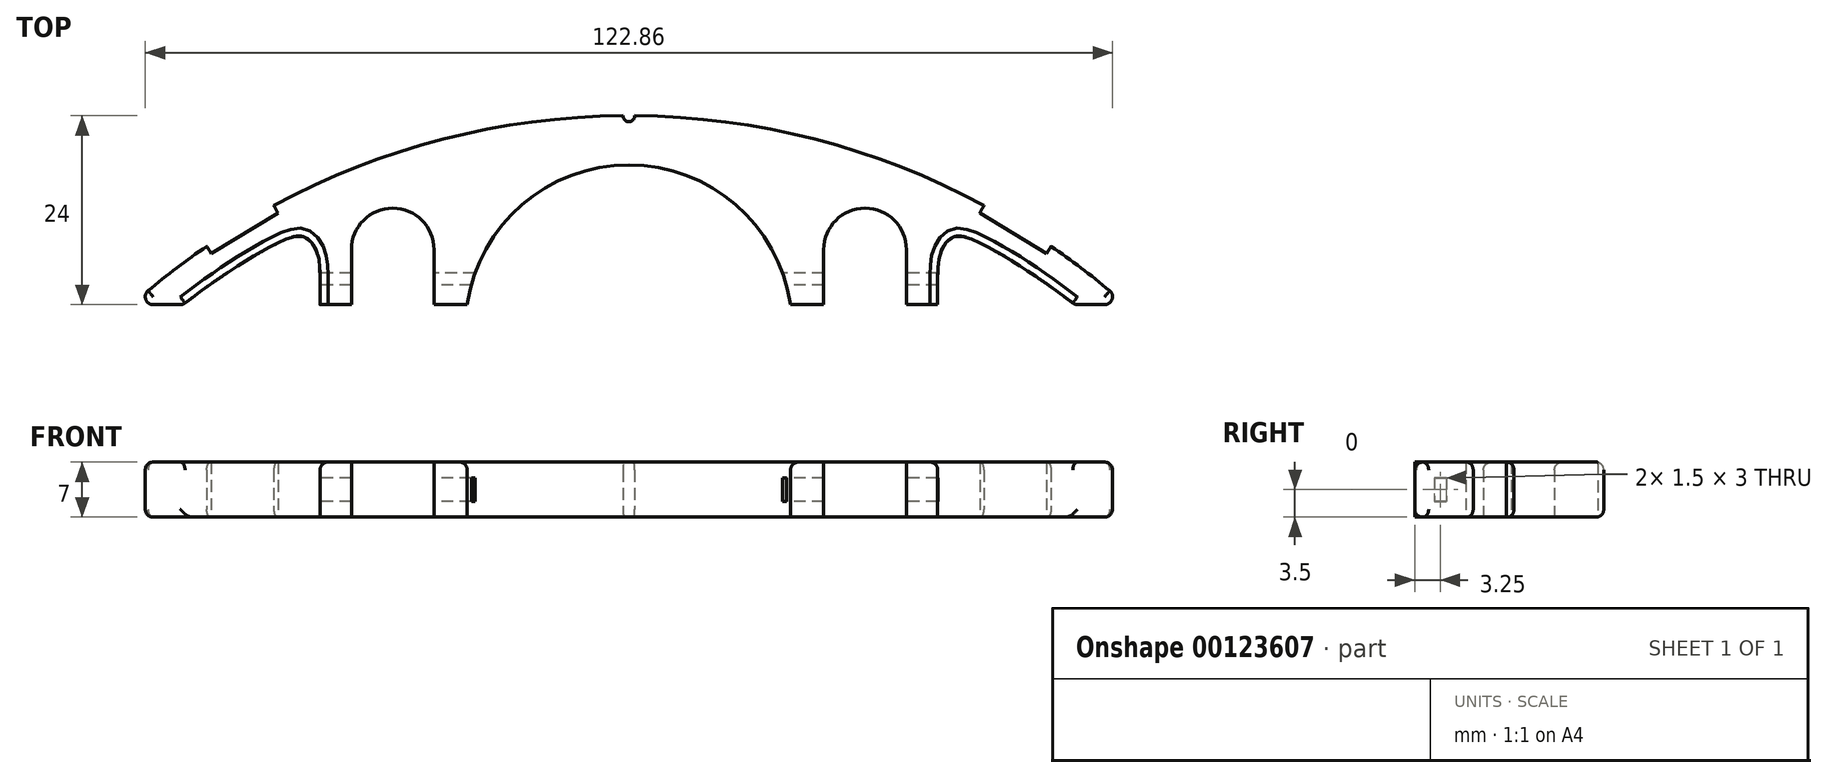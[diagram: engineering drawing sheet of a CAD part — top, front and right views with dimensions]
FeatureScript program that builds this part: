
annotation { "Feature Type Name" : "Feature", "Feature Type Description" : "" }
export const myFeature = defineFeature(function(context is Context, id is Id, definition is map)
    precondition{}
    {
        {
            var Q0;
            Q0=qCreatedBy(makeId("Top.planeOp"),FACE);
            var sketch = newSketch(context, id + "F0", { "sketchPlane" : qUnion([Q0])});
            skCircle(sketch, "E0", {"center": v(0, -78) * mm, "radius": 95 * mm});
            skSolve(sketch);
        }
        {
            var Q0;
            Q0=qCreatedBy(makeId("Top.planeOp"),FACE);
            var sketch = newSketch(context, id + "F1", { "sketchPlane" : qUnion([Q0])});
            skCircle(sketch, "E1", {"center": v(-30, 0) * mm, "radius": 5.25 * mm});
            skSolve(sketch);
        }
        {
            var Q0;
            Q0=qCreatedBy(makeId("Top.planeOp"),FACE);
            var sketch = newSketch(context, id + "F2", { "sketchPlane" : qUnion([Q0])});
            skCircle(sketch, "E2", {"center": v(30, 0) * mm, "radius": 5.25 * mm});
            skSolve(sketch);
        }
        {
            var Q0;
            Q0=qCreatedBy(makeId("Top.planeOp"),FACE);
            var sketch = newSketch(context, id + "F3", { "sketchPlane" : qUnion([Q0])});
            skCircle(sketch, "E3", {"center": v(0, -10) * mm, "radius": 20.75 * mm});
            skSolve(sketch);
        }
        {
            var Q0;
            Q0=qCreatedBy(makeId("Top.planeOp"),FACE);
            var sketch = newSketch(context, id + "F4", { "sketchPlane" : qUnion([Q0])});
            skLineSegment(sketch, "E4.bottom", {"start": v(-90, -20) * mm, "end": v(90, -20) * mm});
            skLineSegment(sketch, "E4.top", {"start": v(-90, -160) * mm, "end": v(90, -160) * mm});
            skLineSegment(sketch, "E4.left", {"start": v(-90, -20) * mm, "end": v(-90, -160) * mm});
            skLineSegment(sketch, "E4.right", {"start": v(90, -20) * mm, "end": v(90, -160) * mm});
            skSolve(sketch);
        }
        {
            var Q0;
            Q0=qCreatedBy(makeId("Top.planeOp"),FACE);
            var sketch = newSketch(context, id + "F5", { "sketchPlane" : qUnion([Q0])});
            skLineSegment(sketch, "E5.bottom", {"start": v(-20.75, -10) * mm, "end": v(20.75, -10) * mm});
            skLineSegment(sketch, "E5.top", {"start": v(-20.75, -51.5) * mm, "end": v(20.75, -51.5) * mm});
            skLineSegment(sketch, "E5.left", {"start": v(-20.75, -10) * mm, "end": v(-20.75, -51.5) * mm});
            skLineSegment(sketch, "E5.right", {"start": v(20.75, -10) * mm, "end": v(20.75, -51.5) * mm});
            skSolve(sketch);
        }
        {
            var Q0;
            Q0=qCreatedBy(makeId("Top.planeOp"),FACE);
            var sketch = newSketch(context, id + "F6", { "sketchPlane" : qUnion([Q0])});
            skLineSegment(sketch, "E6.bottom", {"start": v(-35.25, 0) * mm, "end": v(-24.75, 0) * mm});
            skLineSegment(sketch, "E6.top", {"start": v(-35.25, -25) * mm, "end": v(-24.75, -25) * mm});
            skLineSegment(sketch, "E6.left", {"start": v(-35.25, 0) * mm, "end": v(-35.25, -25) * mm});
            skLineSegment(sketch, "E6.right", {"start": v(-24.75, 0) * mm, "end": v(-24.75, -25) * mm});
            skSolve(sketch);
        }
        {
            var Q0;
            Q0=qCreatedBy(makeId("Top.planeOp"),FACE);
            var sketch = newSketch(context, id + "F7", { "sketchPlane" : qUnion([Q0])});
            skLineSegment(sketch, "E7.bottom", {"start": v(24.75, 0) * mm, "end": v(35.25, 0) * mm});
            skLineSegment(sketch, "E7.top", {"start": v(24.75, -25) * mm, "end": v(35.25, -25) * mm});
            skLineSegment(sketch, "E7.left", {"start": v(24.75, 0) * mm, "end": v(24.75, -25) * mm});
            skLineSegment(sketch, "E7.right", {"start": v(35.25, 0) * mm, "end": v(35.25, -25) * mm});
            skSolve(sketch);
        }
        {
            var Q0;
            Q0=qCreatedBy(makeId("Top.planeOp"),FACE);
            var sketch = newSketch(context, id + "F8", { "sketchPlane" : qUnion([Q0])});
            skCircle(sketch, "E8", {"center": v(0, -155) * mm, "radius": 153 * mm});
            skSolve(sketch);
        }
        {
            var Q0;
            Q0 = qSketchRegion(id + "F0", true);
            extrude(context, id + "F9", {"entities" : qUnion([Q0]), "depth" : 7 * mm});
        }
        {
            var Q0;
            Q0 = qSketchRegion(id + "F1", true);
            var Q1;
            Q1 = qSketchRegion(id + "F2", true);
            var Q2;
            Q2 = qSketchRegion(id + "F3", true);
            var Q3;
            Q3 = qSketchRegion(id + "F4", true);
            var Q4;
            Q4 = qSketchRegion(id + "F6", true);
            var Q5;
            Q5 = qSketchRegion(id + "F7", true);
            var Q6;
            Q6 = qSketchRegion(id + "F5", true);
            extrude(context, id + "F10", {"entities" : qUnion([Q0, Q1, Q2, Q3, Q4, Q5, Q6]), "depth" : 25 * mm});
        }
        {
            var Q0;
            Q0=makeQuery(id+"F10.opExtrude","SWEPT_BODY",BODY,{"disambiguationData":[OSD([sQuery(id+"F1.wireOp",EDGE,"E1")])]});
            var Q1;
            Q1=makeQuery(id+"F10.opExtrude","SWEPT_BODY",BODY,{"disambiguationData":[OSD([sQuery(id+"F2.wireOp",EDGE,"E2")])]});
            var Q2;
            Q2=makeQuery(id+"F10.opExtrude","SWEPT_BODY",BODY,{"disambiguationData":[OSD([sQuery(id+"F3.wireOp",EDGE,"E3")])]});
            var Q3;
            Q3=makeQuery(id+"F10.opExtrude","SWEPT_BODY",BODY,{"disambiguationData":[OSD([sQuery(id+"F4.wireOp",EDGE,"E4.bottom"),sQuery(id+"F4.wireOp",EDGE,"E4.top"),sQuery(id+"F4.wireOp",EDGE,"E4.left"),sQuery(id+"F4.wireOp",EDGE,"E4.right")])]});
            var Q4;
            Q4=makeQuery(id+"F10.opExtrude","SWEPT_BODY",BODY,{"disambiguationData":[OSD([sQuery(id+"F5.wireOp",EDGE,"E5.bottom"),sQuery(id+"F5.wireOp",EDGE,"E5.top"),sQuery(id+"F5.wireOp",EDGE,"E5.left"),sQuery(id+"F5.wireOp",EDGE,"E5.right")])]});
            var Q5;
            Q5=makeQuery(id+"F10.opExtrude","SWEPT_BODY",BODY,{"disambiguationData":[OSD([sQuery(id+"F6.wireOp",EDGE,"E6.bottom"),sQuery(id+"F6.wireOp",EDGE,"E6.top"),sQuery(id+"F6.wireOp",EDGE,"E6.left"),sQuery(id+"F6.wireOp",EDGE,"E6.right")])]});
            var Q6;
            Q6=makeQuery(id+"F10.opExtrude","SWEPT_BODY",BODY,{"disambiguationData":[OSD([sQuery(id+"F7.wireOp",EDGE,"E7.bottom"),sQuery(id+"F7.wireOp",EDGE,"E7.top"),sQuery(id+"F7.wireOp",EDGE,"E7.left"),sQuery(id+"F7.wireOp",EDGE,"E7.right")])]});
            var Q7;
            Q7=makeQuery(id+"F10.opExtrude","SWEPT_BODY",BODY,{"disambiguationData":[OSD([sQuery(id+"F8.wireOp",EDGE,"E8")])]});
            var Q8;
            Q8=makeQuery(id+"F9.opExtrude","SWEPT_BODY",BODY,{"disambiguationData":[OSD([sQuery(id+"F0.wireOp",EDGE,"E0")])]});
            booleanBodies(context, id + "F11", {"operationType" : BooleanOperationType.SUBTRACTION, "tools" : qUnion([Q0, Q1, Q2, Q3, Q4, Q5, Q6, Q7]), "targets" : qUnion([Q8])});
        }
        {
            var Q0;
            Q0=qCreatedBy(makeId("Top.planeOp"),FACE);
            var sketch = newSketch(context, id + "F12", { "sketchPlane" : qUnion([Q0])});
            skFitSpline(sketch, "E9", {"points": [v(-39.25, -8.14) * mm, v(-39.25, -2.66) * mm, v(-39.75, 0) * mm, v(-41.38, 1.65) * mm, v(-44.8, 0.72) * mm, v(-54.39, -5.32) * mm, v(-73.95, -21.45) * mm, v(-74.9, -23.12) * mm, v(-74.82, -24.47) * mm, v(-73.23, -24.63) * mm, v(-58.76, -20.82) * mm, v(-39.95, -12.47) * mm, v(-39.25, -9.82) * mm, v(-39.25, -8.14) * mm]});
            skSolve(sketch);
        }
        {
            var Q0;
            Q0=makeQuery(id+"F12.imprint","IMPRINT",FACE,{"disambiguationData":[TD([[makeQuery(id+"F12.imprint","IMPRINT",EDGE,{"derivedFrom":sQuery(id+"F12.wireOp",EDGE,"E9")}),1.0]])]});
            extrude(context, id + "F13", {"entities" : qUnion([Q0]), "depth" : 25 * mm});
        }
        {
            var Q0;
            Q0=makeQuery(id+"F13.opExtrude","SWEPT_BODY",BODY,{"disambiguationData":[OSD([sQuery(id+"F12.wireOp",EDGE,"E9")])]});
            var Q1;
            Q1=qCreatedBy(makeId("Right.planeOp"),FACE);
            mirror(context, id + "F14", {"entities" : qUnion([Q0]), "mirrorPlane" : qUnion([Q1])});
        }
        {
            var Q0;
            Q0=makeQuery(id+"F13.opExtrude","SWEPT_BODY",BODY,{"disambiguationData":[OSD([sQuery(id+"F12.wireOp",EDGE,"E9")])]});
            var Q1;
            Q1=makeQuery(id+"F14.opPattern","COPY",BODY,{"derivedFrom":makeQuery(id+"F13.opExtrude","SWEPT_BODY",BODY,{"disambiguationData":[OSD([sQuery(id+"F12.wireOp",EDGE,"E9")])]}),"instanceName":"1"});
            var Q2;
            Q2=makeQuery(id+"F9.opExtrude","SWEPT_BODY",BODY,{"disambiguationData":[OSD([sQuery(id+"F0.wireOp",EDGE,"E0")])]});
            booleanBodies(context, id + "F15", {"operationType" : BooleanOperationType.SUBTRACTION, "tools" : qUnion([Q0, Q1]), "targets" : qUnion([Q2])});
        }
        {
            var Q0;
            Q0=makeQuery(id+"F9.opExtrude","CAP_EDGE",EDGE,{"disambiguationData":[OSD([sQuery(id+"F0.wireOp",EDGE,"E0")])],"isStart":false});
            var Q1;
            Q1=makeQuery(id+"F9.opExtrude","CAP_EDGE",EDGE,{"disambiguationData":[OSD([sQuery(id+"F0.wireOp",EDGE,"E0")])],"isStart":true});
            var Q2;
            Q2=makeQuery(id+"F15.opBoolean","INTERSECT",EDGE,{"derivedFrom":[makeQuery(id+"F9.opExtrude","CAP_FACE",FACE,{"disambiguationData":[OSD([sQuery(id+"F0.wireOp",EDGE,"E0")])],"isStart":false}),makeQuery(id+"F14.opPattern","COPY",FACE,{"derivedFrom":makeQuery(id+"F13.opExtrude","SWEPT_FACE",FACE,{"disambiguationData":[OSD([sQuery(id+"F12.wireOp",EDGE,"E9")])]}),"instanceName":"1"})]});
            var Q3;
            Q3=makeQuery(id+"F15.opBoolean","COPY",EDGE,{"derivedFrom":makeQuery(id+"F14.opPattern","COPY",EDGE,{"derivedFrom":makeQuery(id+"F13.opExtrude","CAP_EDGE",EDGE,{"disambiguationData":[OSD([sQuery(id+"F12.wireOp",EDGE,"E9")])],"isStart":true}),"instanceName":"1"})});
            var Q4;
            Q4=makeQuery(id+"F11.opBoolean","INTERSECT",EDGE,{"derivedFrom":[makeQuery(id+"F9.opExtrude","CAP_FACE",FACE,{"disambiguationData":[OSD([sQuery(id+"F0.wireOp",EDGE,"E0")])],"isStart":false}),makeQuery(id+"F10.opExtrude","SWEPT_FACE",FACE,{"disambiguationData":[OSD([sQuery(id+"F3.wireOp",EDGE,"E3")])]})]});
            var Q5;
            Q5=makeQuery(id+"F11.opBoolean","COPY",EDGE,{"derivedFrom":makeQuery(id+"F10.opExtrude","CAP_EDGE",EDGE,{"disambiguationData":[OSD([sQuery(id+"F3.wireOp",EDGE,"E3")])],"isStart":true})});
            var Q6;
            Q6=makeQuery(id+"F15.opBoolean","INTERSECT",EDGE,{"derivedFrom":[makeQuery(id+"F9.opExtrude","CAP_FACE",FACE,{"disambiguationData":[OSD([sQuery(id+"F0.wireOp",EDGE,"E0")])],"isStart":false}),makeQuery(id+"F13.opExtrude","SWEPT_FACE",FACE,{"disambiguationData":[OSD([sQuery(id+"F12.wireOp",EDGE,"E9")])]})]});
            var Q7;
            Q7=makeQuery(id+"F15.opBoolean","COPY",EDGE,{"derivedFrom":makeQuery(id+"F13.opExtrude","CAP_EDGE",EDGE,{"disambiguationData":[OSD([sQuery(id+"F12.wireOp",EDGE,"E9")])],"isStart":true})});
            var Q8;
            Q8=makeQuery(id+"F11.opBoolean","COPY",FACE,{"disambiguationData":[OD(1.0)],"derivedFrom":makeQuery(id+"F10.opExtrude","SWEPT_FACE",FACE,{"disambiguationData":[OSD([sQuery(id+"F4.wireOp",EDGE,"E4.bottom")])]})});
            var Q9;
            Q9=makeQuery(id+"F11.opBoolean","COPY",FACE,{"disambiguationData":[OD(0.0)],"derivedFrom":makeQuery(id+"F10.opExtrude","SWEPT_FACE",FACE,{"disambiguationData":[OSD([sQuery(id+"F4.wireOp",EDGE,"E4.bottom")])]})});
            var Q10;
            {var subQ0=sQuery(id+"F0.wireOp",EDGE,"E0");Q10=makeQuery(id+"F15.opBoolean","SPLIT",FACE,{"disambiguationData":[TD([makeQuery(id+"F9.opExtrude","SWEPT_FACE",FACE,{"disambiguationData":[OSD([subQ0])]})])],"derivedFrom":makeQuery(id+"F11.opBoolean","COPY",FACE,{"disambiguationData":[OD(3.0)],"derivedFrom":makeQuery(id+"F10.opExtrude","SWEPT_FACE",FACE,{"disambiguationData":[OSD([sQuery(id+"F4.wireOp",EDGE,"E4.bottom")])]})})});}
            var Q11;
            {var subQ0=sQuery(id+"F0.wireOp",EDGE,"E0");Q11=makeQuery(id+"F15.opBoolean","SPLIT",FACE,{"disambiguationData":[TD([makeQuery(id+"F9.opExtrude","SWEPT_FACE",FACE,{"disambiguationData":[OSD([subQ0])]})])],"derivedFrom":makeQuery(id+"F11.opBoolean","COPY",FACE,{"disambiguationData":[OD(2.0)],"derivedFrom":makeQuery(id+"F10.opExtrude","SWEPT_FACE",FACE,{"disambiguationData":[OSD([sQuery(id+"F4.wireOp",EDGE,"E4.bottom")])]})})});}
            fillet(context, id + "F16", {"entities" : qUnion([Q0, Q1, Q2, Q3, Q4, Q5, Q6, Q7, Q8, Q9, Q10, Q11]), "radius" : 1 * mm, "tangentPropagation" : true, "allowEdgeOverflow" : false});
        }
        {
            var Q0;
            Q0=qCreatedBy(makeId("Right.planeOp"),FACE);
            var sketch = newSketch(context, id + "F17", { "sketchPlane" : qUnion([Q0])});
            skLineSegment(sketch, "E10.bottom", {"start": v(-4.5, 5) * mm, "end": v(-3, 5) * mm});
            skLineSegment(sketch, "E10.top", {"start": v(-4.5, 2) * mm, "end": v(-3, 2) * mm});
            skLineSegment(sketch, "E10.left", {"start": v(-4.5, 5) * mm, "end": v(-4.5, 2) * mm});
            skLineSegment(sketch, "E10.right", {"start": v(-3, 5) * mm, "end": v(-3, 2) * mm});
            skSolve(sketch);
        }
        {
            var Q0;
            Q0 = qSketchRegion(id + "F17", true);
            extrude(context, id + "F18", {"entities" : qUnion([Q0]), "endBound" : BoundingType.SYMMETRIC, "depth" : 80 * mm});
        }
        {
            var Q0;
            Q0=qCreatedBy(makeId("Top.planeOp"),FACE);
            var sketch = newSketch(context, id + "F19", { "sketchPlane" : qUnion([Q0])});
            skLineSegment(sketch, "E11.bottom", {"start": v(-45, 18) * mm, "end": v(45, 18) * mm});
            skLineSegment(sketch, "E11.top", {"start": v(-45, -7) * mm, "end": v(45, -7) * mm});
            skLineSegment(sketch, "E11.left", {"start": v(-45, 18) * mm, "end": v(-45, -7) * mm});
            skLineSegment(sketch, "E11.right", {"start": v(45, 18) * mm, "end": v(45, -7) * mm});
            skSolve(sketch);
        }
        {
            var Q0;
            Q0=makeQuery(id+"F19.imprint","IMPRINT",FACE,{"disambiguationData":[TD([[makeQuery(id+"F19.imprint","IMPRINT",EDGE,{"derivedFrom":sQuery(id+"F19.wireOp",EDGE,"E11.bottom")}),-1.0]])]});
            extrude(context, id + "F20", {"entities" : qUnion([Q0]), "depth" : 25 * mm});
        }
        {
            var Q0;
            Q0=makeQuery(id+"F8.imprint","IMPRINT",FACE,{"disambiguationData":[TD([[makeQuery(id+"F8.imprint","IMPRINT",EDGE,{"derivedFrom":sQuery(id+"F8.wireOp",EDGE,"E8")}),1.0]])]});
            extrude(context, id + "F21", {"entities" : qUnion([Q0]), "depth" : 25 * mm});
        }
        {
            var Q0;
            Q0=makeQuery(id+"F20.opExtrude","SWEPT_BODY",BODY,{"disambiguationData":[OSD([sQuery(id+"F19.wireOp",EDGE,"E11.bottom"),sQuery(id+"F19.wireOp",EDGE,"E11.top"),sQuery(id+"F19.wireOp",EDGE,"E11.left"),sQuery(id+"F19.wireOp",EDGE,"E11.right")])]});
            var Q1;
            Q1=makeQuery(id+"F21.opExtrude","SWEPT_BODY",BODY,{"disambiguationData":[OSD([sQuery(id+"F8.wireOp",EDGE,"E8")])]});
            booleanBodies(context, id + "F22", {"operationType" : BooleanOperationType.SUBTRACTION, "tools" : qUnion([Q0]), "targets" : qUnion([Q1])});
        }
        {
            var Q0;
            Q0=makeQuery(id+"F21.opExtrude","SWEPT_BODY",BODY,{"disambiguationData":[OSD([sQuery(id+"F8.wireOp",EDGE,"E8")])]});
            var Q1;
            Q1=makeQuery(id+"F11.opBoolean","SPLIT",BODY,{"disambiguationData":[OD(1.0)],"derivedFrom":makeQuery(id+"F9.opExtrude","SWEPT_BODY",BODY,{"disambiguationData":[OSD([sQuery(id+"F0.wireOp",EDGE,"E0")])]})});
            var Q2;
            Q2=makeQuery(id+"F11.opBoolean","SPLIT",BODY,{"disambiguationData":[OD(2.0)],"derivedFrom":makeQuery(id+"F9.opExtrude","SWEPT_BODY",BODY,{"disambiguationData":[OSD([sQuery(id+"F0.wireOp",EDGE,"E0")])]})});
            var Q3;
            Q3=makeQuery(id+"F11.opBoolean","SPLIT",BODY,{"disambiguationData":[OD(3.0)],"derivedFrom":makeQuery(id+"F9.opExtrude","SWEPT_BODY",BODY,{"disambiguationData":[OSD([sQuery(id+"F0.wireOp",EDGE,"E0")])]})});
            var Q4;
            Q4=makeQuery(id+"F11.opBoolean","SPLIT",BODY,{"disambiguationData":[OD(0.0)],"derivedFrom":makeQuery(id+"F9.opExtrude","SWEPT_BODY",BODY,{"disambiguationData":[OSD([sQuery(id+"F0.wireOp",EDGE,"E0")])]})});
            booleanBodies(context, id + "F23", {"operationType" : BooleanOperationType.SUBTRACTION, "tools" : qUnion([Q0]), "targets" : qUnion([Q1, Q2, Q3, Q4])});
        }
        {
            var Q0;
            Q0=makeQuery(id+"F18.opExtrude","SWEPT_BODY",BODY,{"disambiguationData":[OSD([sQuery(id+"F17.wireOp",EDGE,"E10.bottom"),sQuery(id+"F17.wireOp",EDGE,"E10.top"),sQuery(id+"F17.wireOp",EDGE,"E10.left"),sQuery(id+"F17.wireOp",EDGE,"E10.right")])]});
            var Q1;
            Q1=makeQuery(id+"F11.opBoolean","SPLIT",BODY,{"disambiguationData":[OD(3.0)],"derivedFrom":makeQuery(id+"F9.opExtrude","SWEPT_BODY",BODY,{"disambiguationData":[OSD([sQuery(id+"F0.wireOp",EDGE,"E0")])]})});
            booleanBodies(context, id + "F24", {"operationType" : BooleanOperationType.SUBTRACTION, "tools" : qUnion([Q0]), "targets" : qUnion([Q1])});
        }
        {
            var Q0;
            Q0=qCreatedBy(makeId("Top.planeOp"),FACE);
            var sketch = newSketch(context, id + "F25", { "sketchPlane" : qUnion([Q0])});
            skCircle(sketch, "E12", {"center": v(0, 17) * mm, "radius": 0.75 * mm});
            skSolve(sketch);
        }
        {
            var Q0;
            Q0=makeQuery(id+"F25.imprint","IMPRINT",FACE,{"disambiguationData":[TD([[makeQuery(id+"F25.imprint","IMPRINT",EDGE,{"derivedFrom":sQuery(id+"F25.wireOp",EDGE,"E12")}),1.0]])]});
            extrude(context, id + "F26", {"entities" : qUnion([Q0]), "depth" : 25 * mm});
        }
        {
            var Q0;
            Q0=makeQuery(id+"F26.opExtrude","SWEPT_BODY",BODY,{"disambiguationData":[OSD([sQuery(id+"F25.wireOp",EDGE,"E12")])]});
            var Q1;
            Q1=makeQuery(id+"F11.opBoolean","SPLIT",BODY,{"disambiguationData":[OD(3.0)],"derivedFrom":makeQuery(id+"F9.opExtrude","SWEPT_BODY",BODY,{"disambiguationData":[OSD([sQuery(id+"F0.wireOp",EDGE,"E0")])]})});
            booleanBodies(context, id + "F27", {"operationType" : BooleanOperationType.SUBTRACTION, "tools" : qUnion([Q0]), "targets" : qUnion([Q1])});
        }
        {
            var Q0;
            Q0=qCreatedBy(makeId("Top.planeOp"),FACE);
            var sketch = newSketch(context, id + "F28", { "sketchPlane" : qUnion([Q0])});
            skLineSegment(sketch, "E13", {"start": v(0, 17) * mm, "end": v(0, -78) * mm});
            skLineSegment(sketch, "E14", {"start": v(0, -78) * mm, "end": v(45.98, 5.13) * mm});
            skLineSegment(sketch, "E15", {"start": v(45.98, 5.13) * mm, "end": v(0, 17) * mm});
            skSolve(sketch);
        }
        {
            var Q0;
            Q0=qCreatedBy(makeId("Top.planeOp"),FACE);
            var sketch = newSketch(context, id + "F29", { "sketchPlane" : qUnion([Q0])});
            skLineSegment(sketch, "E16", {"start": v(45.46, 6.23) * mm, "end": v(54, 1.02) * mm});
            skLineSegment(sketch, "E17", {"start": v(54, 1.02) * mm, "end": v(53.05, -0.52) * mm});
            skLineSegment(sketch, "E18", {"start": v(53.05, -0.52) * mm, "end": v(44.57, 4.65) * mm});
            skLineSegment(sketch, "E19", {"start": v(44.57, 4.65) * mm, "end": v(45.46, 6.23) * mm});
            skSolve(sketch);
        }
        {
            var Q0;
            Q0=makeQuery(id+"F29.imprint","IMPRINT",FACE,{"disambiguationData":[TD([[makeQuery(id+"F29.imprint","IMPRINT",EDGE,{"derivedFrom":sQuery(id+"F29.wireOp",EDGE,"E16")}),-1.0]])]});
            extrude(context, id + "F30", {"entities" : qUnion([Q0]), "depth" : 25 * mm});
        }
        {
            var Q0;
            Q0=makeQuery(id+"F30.opExtrude","SWEPT_BODY",BODY,{"disambiguationData":[OSD([sQuery(id+"F29.wireOp",EDGE,"E16"),sQuery(id+"F29.wireOp",EDGE,"E17"),sQuery(id+"F29.wireOp",EDGE,"E18"),sQuery(id+"F29.wireOp",EDGE,"E19")])]});
            var Q1;
            Q1=qCreatedBy(makeId("Right.planeOp"),FACE);
            mirror(context, id + "F31", {"entities" : qUnion([Q0]), "mirrorPlane" : qUnion([Q1])});
        }
        {
            var Q0;
            Q0=makeQuery(id+"F30.opExtrude","SWEPT_BODY",BODY,{"disambiguationData":[OSD([sQuery(id+"F29.wireOp",EDGE,"E16"),sQuery(id+"F29.wireOp",EDGE,"E17"),sQuery(id+"F29.wireOp",EDGE,"E18"),sQuery(id+"F29.wireOp",EDGE,"E19")])]});
            var Q1;
            Q1=makeQuery(id+"F31.opPattern","COPY",BODY,{"derivedFrom":makeQuery(id+"F30.opExtrude","SWEPT_BODY",BODY,{"disambiguationData":[OSD([sQuery(id+"F29.wireOp",EDGE,"E16"),sQuery(id+"F29.wireOp",EDGE,"E17"),sQuery(id+"F29.wireOp",EDGE,"E18"),sQuery(id+"F29.wireOp",EDGE,"E19")])]}),"instanceName":"1"});
            var Q2;
            Q2=makeQuery(id+"F11.opBoolean","SPLIT",BODY,{"disambiguationData":[OD(3.0)],"derivedFrom":makeQuery(id+"F9.opExtrude","SWEPT_BODY",BODY,{"disambiguationData":[OSD([sQuery(id+"F0.wireOp",EDGE,"E0")])]})});
            booleanBodies(context, id + "F32", {"operationType" : BooleanOperationType.SUBTRACTION, "tools" : qUnion([Q0, Q1]), "targets" : qUnion([Q2])});
        }
        {
            var Q0;
            Q0=qCreatedBy(makeId("Top.planeOp"),FACE);
            var sketch = newSketch(context, id + "F33", { "sketchPlane" : qUnion([Q0])});
            skLineSegment(sketch, "E20.bottom", {"start": v(-90.31, -7) * mm, "end": v(89.69, -7) * mm});
            skLineSegment(sketch, "E20.top", {"start": v(-90.31, -48.25) * mm, "end": v(89.69, -48.25) * mm});
            skLineSegment(sketch, "E20.left", {"start": v(-90.31, -7) * mm, "end": v(-90.31, -48.25) * mm});
            skLineSegment(sketch, "E20.right", {"start": v(89.69, -7) * mm, "end": v(89.69, -48.25) * mm});
            skSolve(sketch);
        }
        {
            var Q0;
            Q0=makeQuery(id+"F33.imprint","IMPRINT",FACE,{"disambiguationData":[TD([[makeQuery(id+"F33.imprint","IMPRINT",EDGE,{"derivedFrom":sQuery(id+"F33.wireOp",EDGE,"E20.bottom")}),-1.0]])]});
            extrude(context, id + "F34", {"entities" : qUnion([Q0]), "depth" : 25 * mm});
        }
        {
            var Q0;
            Q0=makeQuery(id+"F34.opExtrude","SWEPT_BODY",BODY,{"disambiguationData":[OSD([sQuery(id+"F33.wireOp",EDGE,"E20.bottom"),sQuery(id+"F33.wireOp",EDGE,"E20.top"),sQuery(id+"F33.wireOp",EDGE,"E20.left"),sQuery(id+"F33.wireOp",EDGE,"E20.right")])]});
            var Q1;
            Q1=makeQuery(id+"F11.opBoolean","SPLIT",BODY,{"disambiguationData":[OD(3.0)],"derivedFrom":makeQuery(id+"F9.opExtrude","SWEPT_BODY",BODY,{"disambiguationData":[OSD([sQuery(id+"F0.wireOp",EDGE,"E0")])]})});
            booleanBodies(context, id + "F35", {"operationType" : BooleanOperationType.SUBTRACTION, "tools" : qUnion([Q0]), "targets" : qUnion([Q1])});
        }
        {
            var Q0;
            Q0=makeQuery(id+"F35.opBoolean","COPY",FACE,{"disambiguationData":[OD(1.0)],"derivedFrom":makeQuery(id+"F34.opExtrude","SWEPT_FACE",FACE,{"disambiguationData":[OSD([sQuery(id+"F33.wireOp",EDGE,"E20.bottom")])]})});
            var Q1;
            Q1=makeQuery(id+"F35.opBoolean","COPY",FACE,{"disambiguationData":[OD(0.0)],"derivedFrom":makeQuery(id+"F34.opExtrude","SWEPT_FACE",FACE,{"disambiguationData":[OSD([sQuery(id+"F33.wireOp",EDGE,"E20.bottom")])]})});
            fillet(context, id + "F36", {"entities" : qUnion([Q0, Q1]), "radius" : 1 * mm, "tangentPropagation" : true, "allowEdgeOverflow" : false});
        }
    });
